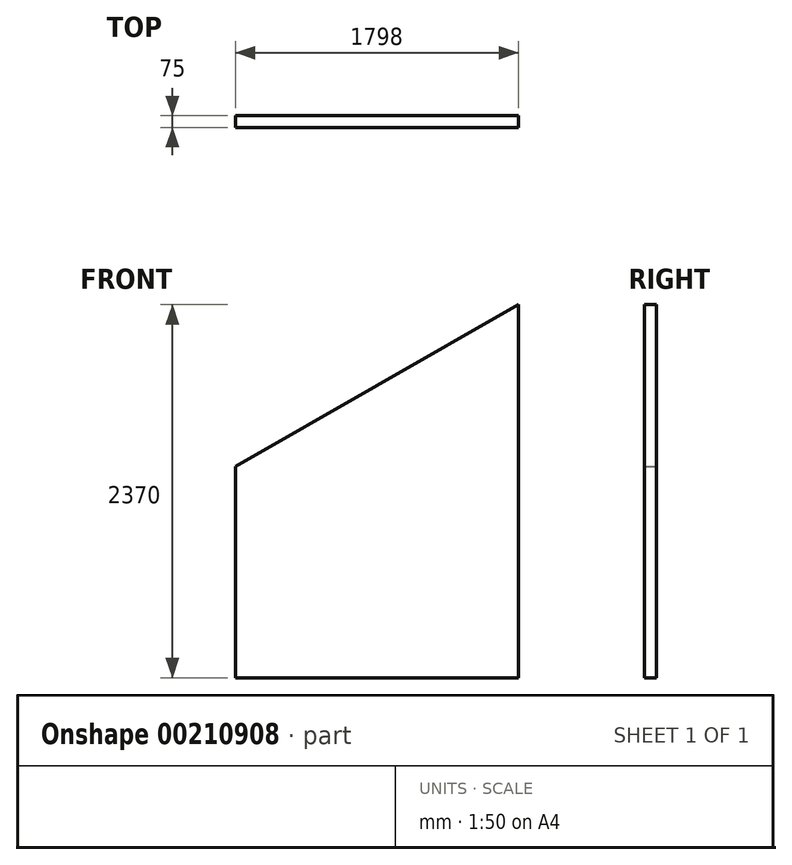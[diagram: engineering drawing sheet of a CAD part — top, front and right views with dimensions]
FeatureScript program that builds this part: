
annotation { "Feature Type Name" : "Feature", "Feature Type Description" : "" }
export const myFeature = defineFeature(function(context is Context, id is Id, definition is map)
    precondition{}
    {
        {
            var Q0;
            Q0=qCreatedBy(makeId("Front.planeOp"),FACE);
            var sketch = newSketch(context, id + "F0", { "sketchPlane" : qUnion([Q0])});
            skLineSegment(sketch, "E0.bottom", {"start": v(0, 0) * mm, "end": v(1798, 0) * mm});
            skLineSegment(sketch, "E0.right", {"start": v(1798, 0) * mm, "end": v(1798, 2370) * mm});
            skLineSegment(sketch, "E1", {"start": v(0, 1342) * mm, "end": v(1798, 2370) * mm});
            skLineSegment(sketch, "E2", {"start": v(0, 0) * mm, "end": v(0, 1342) * mm});
            skSolve(sketch);
        }
        {
            var Q0;
            Q0=makeQuery(id+"F0.imprint","IMPRINT",FACE,{"disambiguationData":[TD([[makeQuery(id+"F0.imprint","IMPRINT",EDGE,{"derivedFrom":sQuery(id+"F0.wireOp",EDGE,"E0.bottom")}),1.0]])]});
            extrude(context, id + "F1", {"entities" : qUnion([Q0]), "depth" : 75 * mm});
        }
    });
